# Revit family: RN 81046 Optipress-Aquaplus-Vis de rappel
name_source: partatom
category: Rohrformteile
units: mm (PartAtom-declared; Revit-internal decimal feet)

## family parameters
Arbeitsebenenbasiert = Nein
Beim Laden mit Abzugskörper schneiden = Nein
Bemaßung runder Anschluss = Durchmesser verwenden
Gemeinsam genutzt = Nein
Immer vertikal = Ja
Teiletyp = Verbindung

## types (12) — shared parameters
1.010.00.2 Numéro de feuille de la directive = 29
1.010.00.3 Date de publication (mois) de la ligne directrice = 201308
1.010.00.4 Nom du Fabricant = R. Nussbaum AG
1.010.00.5 Date de révision du fichier = 20190521
1.010.00.6 Adresse Web du fabricant = http://www.nussbaum.ch
1.100.00.4 Désignation du produit = Alimentation
1.110.00.2 Indice = 4
1.110.00.4 Désignation du produit = Optipress
1.960/3L.00.8 Lien (URL) = https://www.nussbaum.ch
29.700.00.4 Nom du produit = Optipress-Aquaplus-Vis de rappel, avec filetage mâle
29.700.00.5 Identification du produit = 2
29.700.00.6 Forme transversale = 1
29.700.00.7 Système de taille nominale = DN
29.700.00.8 Système de pression nominale = PN
29.710.02.4 Pression nominale = 16
29.710.02.5 Max. [hPa] = 1600
29.710.02.7 Max. [hPa] = 1600
29.710.02.9 Max. [°C] = 95
Connector Visibility = Nein
EnclosingSpace Visibility = Nein

## per-type parameters (varying)
- 81046.21, Optipress-Aquaplus-Vis de rappel, avec filetage mâle, DN=15x20, L=67, R=¾: 1.800.00.3 Numéro BS=01900400000000000000000000000000000000000000000028000000000000000012; 1.810.00.3 Numéro de commande fabricant=81046.21; 1.810.00.4 Numéro DATANORM=81046.21; 1.810.00.6 Numéro GTIN=7612945022196; 29.710.02.10 Poids d'ajustement [kg]=0.139; 29.710.02.3 La désignation=Optipress-Aquaplus-Vis de rappel, avec filetage mâle, DN=15x20, L=67, R=¾; CONNECTOR0_DIAMETER_dX_0r=15 mm  [stored 0.0492126 ft]; CONNECTOR0_dX_01=22 mm; CONNECTOR0_ref_dX=22 mm; CONNECTOR1_DIAMETER_dX_0r=20 mm; CONNECTOR1_dX_00=48 mm; CONNECTOR1_dX_01=63 mm; CONNECTOR1_ref_dX=48 mm; R. Nussbaum AG 81046.20 fr Visibility=Nein; R. Nussbaum AG 81046.21 fr Visibility=Ja; R. Nussbaum AG 81046.22 fr Visibility=Nein; R. Nussbaum AG 81046.23 fr Visibility=Nein; R. Nussbaum AG 81046.24 fr Visibility=Nein; R. Nussbaum AG 81046.25 fr Visibility=Nein; R. Nussbaum AG 81046.27 fr Visibility=Nein; R. Nussbaum AG 81046.28 fr Visibility=Nein; R. Nussbaum AG 81046.29 fr Visibility=Nein; R. Nussbaum AG 81046.31 fr Visibility=Nein; R. Nussbaum AG 81046.33 fr Visibility=Nein; R. Nussbaum AG 81046.34 fr Visibility=Nein
- 81046.22, Optipress-Aquaplus-Vis de rappel, avec filetage mâle, DN=15, L=67, R=½: 1.800.00.3 Numéro BS=01900400000000000000000000000000000000000000000028000000000000000013; 1.810.00.3 Numéro de commande fabricant=81046.22; 1.810.00.4 Numéro DATANORM=81046.22; 1.810.00.5 Numéro StLB=266.333; 1.810.00.6 Numéro GTIN=7612945022202; 29.710.02.10 Poids d'ajustement [kg]=0.129; 29.710.02.3 La désignation=Optipress-Aquaplus-Vis de rappel, avec filetage mâle, DN=15, L=67, R=½; CONNECTOR0_DIAMETER_dX_0r=15 mm  [stored 0.0492126 ft]; CONNECTOR0_dX_01=22 mm; CONNECTOR0_ref_dX=22 mm; CONNECTOR1_DIAMETER_dX_0r=15 mm  [stored 0.0492126 ft]; CONNECTOR1_dX_00=50 mm; CONNECTOR1_dX_01=63 mm; CONNECTOR1_ref_dX=50 mm; R. Nussbaum AG 81046.20 fr Visibility=Nein; R. Nussbaum AG 81046.21 fr Visibility=Nein; R. Nussbaum AG 81046.22 fr Visibility=Ja; R. Nussbaum AG 81046.23 fr Visibility=Nein; R. Nussbaum AG 81046.24 fr Visibility=Nein; R. Nussbaum AG 81046.25 fr Visibility=Nein; R. Nussbaum AG 81046.27 fr Visibility=Nein; R. Nussbaum AG 81046.28 fr Visibility=Nein; R. Nussbaum AG 81046.29 fr Visibility=Nein; R. Nussbaum AG 81046.31 fr Visibility=Nein; R. Nussbaum AG 81046.33 fr Visibility=Nein; R. Nussbaum AG 81046.34 fr Visibility=Nein
- 81046.23, Optipress-Aquaplus-Vis de rappel, avec filetage mâle, DN=15x20, L=69, R=¾: 1.800.00.3 Numéro BS=01900400000000000000000000000000000000000000000028000000000000000014; 1.810.00.3 Numéro de commande fabricant=81046.23; 1.810.00.4 Numéro DATANORM=81046.23; 1.810.00.6 Numéro GTIN=7612945022219; 29.710.02.10 Poids d'ajustement [kg]=0.139; 29.710.02.3 La désignation=Optipress-Aquaplus-Vis de rappel, avec filetage mâle, DN=15x20, L=69, R=¾; CONNECTOR0_DIAMETER_dX_0r=15 mm  [stored 0.0492126 ft]; CONNECTOR0_dX_01=22 mm; CONNECTOR0_ref_dX=22 mm; CONNECTOR1_DIAMETER_dX_0r=20 mm; CONNECTOR1_dX_00=50 mm; CONNECTOR1_dX_01=65 mm; CONNECTOR1_ref_dX=50 mm; R. Nussbaum AG 81046.20 fr Visibility=Nein; R. Nussbaum AG 81046.21 fr Visibility=Nein; R. Nussbaum AG 81046.22 fr Visibility=Nein; R. Nussbaum AG 81046.23 fr Visibility=Ja; R. Nussbaum AG 81046.24 fr Visibility=Nein; R. Nussbaum AG 81046.25 fr Visibility=Nein; R. Nussbaum AG 81046.27 fr Visibility=Nein; R. Nussbaum AG 81046.28 fr Visibility=Nein; R. Nussbaum AG 81046.29 fr Visibility=Nein; R. Nussbaum AG 81046.31 fr Visibility=Nein; R. Nussbaum AG 81046.33 fr Visibility=Nein; R. Nussbaum AG 81046.34 fr Visibility=Nein
- 81046.24, Optipress-Aquaplus-Vis de rappel, avec filetage mâle, DN=20x15, L=80, R=½: 1.800.00.3 Numéro BS=01900400000000000000000000000000000000000000000028000000000000000015; 1.810.00.3 Numéro de commande fabricant=81046.24; 1.810.00.4 Numéro DATANORM=81046.24; 1.810.00.6 Numéro GTIN=7612945022226; 29.710.02.10 Poids d'ajustement [kg]=0.149; 29.710.02.3 La désignation=Optipress-Aquaplus-Vis de rappel, avec filetage mâle, DN=20x15, L=80, R=½; CONNECTOR0_DIAMETER_dX_0r=20 mm; CONNECTOR0_dX_01=24 mm; CONNECTOR0_ref_dX=24 mm; CONNECTOR1_DIAMETER_dX_0r=15 mm  [stored 0.0492126 ft]; CONNECTOR1_dX_00=58 mm; CONNECTOR1_dX_01=71 mm; CONNECTOR1_ref_dX=58 mm; R. Nussbaum AG 81046.20 fr Visibility=Nein; R. Nussbaum AG 81046.21 fr Visibility=Nein; R. Nussbaum AG 81046.22 fr Visibility=Nein; R. Nussbaum AG 81046.23 fr Visibility=Nein; R. Nussbaum AG 81046.24 fr Visibility=Ja; R. Nussbaum AG 81046.25 fr Visibility=Nein; R. Nussbaum AG 81046.27 fr Visibility=Nein; R. Nussbaum AG 81046.28 fr Visibility=Nein; R. Nussbaum AG 81046.29 fr Visibility=Nein; R. Nussbaum AG 81046.31 fr Visibility=Nein; R. Nussbaum AG 81046.33 fr Visibility=Nein; R. Nussbaum AG 81046.34 fr Visibility=Nein
- 81046.25, Optipress-Aquaplus-Vis de rappel, avec filetage mâle, DN=20, L=81, R=¾: 1.800.00.3 Numéro BS=01900400000000000000000000000000000000000000000028000000000000000016; 1.810.00.3 Numéro de commande fabricant=81046.25; 1.810.00.4 Numéro DATANORM=81046.25; 1.810.00.5 Numéro StLB=266.334; 1.810.00.6 Numéro GTIN=7612945022233; 29.710.02.10 Poids d'ajustement [kg]=0.209; 29.710.02.3 La désignation=Optipress-Aquaplus-Vis de rappel, avec filetage mâle, DN=20, L=81, R=¾; CONNECTOR0_DIAMETER_dX_0r=20 mm; CONNECTOR0_dX_01=24 mm; CONNECTOR0_ref_dX=24 mm; CONNECTOR1_DIAMETER_dX_0r=20 mm; CONNECTOR1_dX_00=53 mm; CONNECTOR1_dX_01=68 mm; CONNECTOR1_ref_dX=53 mm; R. Nussbaum AG 81046.20 fr Visibility=Nein; R. Nussbaum AG 81046.21 fr Visibility=Nein; R. Nussbaum AG 81046.22 fr Visibility=Nein; R. Nussbaum AG 81046.23 fr Visibility=Nein; R. Nussbaum AG 81046.24 fr Visibility=Nein; R. Nussbaum AG 81046.25 fr Visibility=Ja; R. Nussbaum AG 81046.27 fr Visibility=Nein; R. Nussbaum AG 81046.28 fr Visibility=Nein; R. Nussbaum AG 81046.29 fr Visibility=Nein; R. Nussbaum AG 81046.31 fr Visibility=Nein; R. Nussbaum AG 81046.33 fr Visibility=Nein; R. Nussbaum AG 81046.34 fr Visibility=Nein
- 81046.27, Optipress-Aquaplus-Vis de rappel, avec filetage mâle, DN=20x25, L=84, R=1: 1.800.00.3 Numéro BS=01900400000000000000000000000000000000000000000028000000000000000017; 1.810.00.3 Numéro de commande fabricant=81046.27; 1.810.00.4 Numéro DATANORM=81046.27; 1.810.00.6 Numéro GTIN=7612945022240; 29.710.02.10 Poids d'ajustement [kg]=0.212; 29.710.02.3 La désignation=Optipress-Aquaplus-Vis de rappel, avec filetage mâle, DN=20x25, L=84, R=1; CONNECTOR0_DIAMETER_dX_0r=20 mm; CONNECTOR0_dX_01=24 mm; CONNECTOR0_ref_dX=24 mm; CONNECTOR1_DIAMETER_dX_0r=25 mm  [stored 0.082021 ft]; CONNECTOR1_dX_00=54 mm; CONNECTOR1_dX_01=71 mm; CONNECTOR1_ref_dX=54 mm; R. Nussbaum AG 81046.20 fr Visibility=Nein; R. Nussbaum AG 81046.21 fr Visibility=Nein; R. Nussbaum AG 81046.22 fr Visibility=Nein; R. Nussbaum AG 81046.23 fr Visibility=Nein; R. Nussbaum AG 81046.24 fr Visibility=Nein; R. Nussbaum AG 81046.25 fr Visibility=Nein; R. Nussbaum AG 81046.27 fr Visibility=Ja; R. Nussbaum AG 81046.28 fr Visibility=Nein; R. Nussbaum AG 81046.29 fr Visibility=Nein; R. Nussbaum AG 81046.31 fr Visibility=Nein; R. Nussbaum AG 81046.33 fr Visibility=Nein; R. Nussbaum AG 81046.34 fr Visibility=Nein
- 81046.28, Optipress-Aquaplus-Vis de rappel, avec filetage mâle, DN=25x20, L=82, R=¾: 1.800.00.3 Numéro BS=01900400000000000000000000000000000000000000000028000000000000000018; 1.810.00.3 Numéro de commande fabricant=81046.28; 1.810.00.4 Numéro DATANORM=81046.28; 1.810.00.6 Numéro GTIN=7612945682802; 29.710.02.10 Poids d'ajustement [kg]=0.319; 29.710.02.3 La désignation=Optipress-Aquaplus-Vis de rappel, avec filetage mâle, DN=25x20, L=82, R=¾; CONNECTOR0_DIAMETER_dX_0r=25 mm  [stored 0.082021 ft]; CONNECTOR0_dX_01=24 mm; CONNECTOR0_ref_dX=24 mm; CONNECTOR1_DIAMETER_dX_0r=20 mm; CONNECTOR1_dX_00=64 mm; CONNECTOR1_dX_01=79 mm; CONNECTOR1_ref_dX=64 mm; R. Nussbaum AG 81046.20 fr Visibility=Nein; R. Nussbaum AG 81046.21 fr Visibility=Nein; R. Nussbaum AG 81046.22 fr Visibility=Nein; R. Nussbaum AG 81046.23 fr Visibility=Nein; R. Nussbaum AG 81046.24 fr Visibility=Nein; R. Nussbaum AG 81046.25 fr Visibility=Nein; R. Nussbaum AG 81046.27 fr Visibility=Nein; R. Nussbaum AG 81046.28 fr Visibility=Ja; R. Nussbaum AG 81046.29 fr Visibility=Nein; R. Nussbaum AG 81046.31 fr Visibility=Nein; R. Nussbaum AG 81046.33 fr Visibility=Nein; R. Nussbaum AG 81046.34 fr Visibility=Nein
- 81046.29, Optipress-Aquaplus-Vis de rappel, avec filetage mâle, DN=25, L=78, R=1: 1.800.00.3 Numéro BS=01900400000000000000000000000000000000000000000028000000000000000019; 1.810.00.3 Numéro de commande fabricant=81046.29; 1.810.00.4 Numéro DATANORM=81046.29; 1.810.00.5 Numéro StLB=266.335; 1.810.00.6 Numéro GTIN=7612945022257; 29.710.02.10 Poids d'ajustement [kg]=0.311; 29.710.02.3 La désignation=Optipress-Aquaplus-Vis de rappel, avec filetage mâle, DN=25, L=78, R=1; CONNECTOR0_DIAMETER_dX_0r=25 mm  [stored 0.082021 ft]; CONNECTOR0_dX_01=24 mm; CONNECTOR0_ref_dX=24 mm; CONNECTOR1_DIAMETER_dX_0r=25 mm  [stored 0.082021 ft]; CONNECTOR1_dX_00=58 mm; CONNECTOR1_dX_01=75 mm; CONNECTOR1_ref_dX=58 mm; R. Nussbaum AG 81046.20 fr Visibility=Nein; R. Nussbaum AG 81046.21 fr Visibility=Nein; R. Nussbaum AG 81046.22 fr Visibility=Nein; R. Nussbaum AG 81046.23 fr Visibility=Nein; R. Nussbaum AG 81046.24 fr Visibility=Nein; R. Nussbaum AG 81046.25 fr Visibility=Nein; R. Nussbaum AG 81046.27 fr Visibility=Nein; R. Nussbaum AG 81046.28 fr Visibility=Nein; R. Nussbaum AG 81046.29 fr Visibility=Ja; R. Nussbaum AG 81046.31 fr Visibility=Nein; R. Nussbaum AG 81046.33 fr Visibility=Nein; R. Nussbaum AG 81046.34 fr Visibility=Nein
- 81046.31, Optipress-Aquaplus-Vis de rappel, avec filetage mâle, DN=32, L=101, R=1¼: 1.800.00.3 Numéro BS=01900400000000000000000000000000000000000000000028000000000000000020; 1.810.00.3 Numéro de commande fabricant=81046.31; 1.810.00.4 Numéro DATANORM=81046.31; 1.810.00.5 Numéro StLB=266.336; 1.810.00.6 Numéro GTIN=7612945022264; 29.710.02.10 Poids d'ajustement [kg]=0.439; 29.710.02.3 La désignation=Optipress-Aquaplus-Vis de rappel, avec filetage mâle, DN=32, L=101, R=1¼; CONNECTOR0_DIAMETER_dX_0r=32 mm  [stored 0.104987 ft]; CONNECTOR0_dX_01=26 mm; CONNECTOR0_ref_dX=26 mm; CONNECTOR1_DIAMETER_dX_0r=32 mm  [stored 0.104987 ft]; CONNECTOR1_dX_00=66 mm; CONNECTOR1_dX_01=85 mm; CONNECTOR1_ref_dX=66 mm; R. Nussbaum AG 81046.20 fr Visibility=Nein; R. Nussbaum AG 81046.21 fr Visibility=Nein; R. Nussbaum AG 81046.22 fr Visibility=Nein; R. Nussbaum AG 81046.23 fr Visibility=Nein; R. Nussbaum AG 81046.24 fr Visibility=Nein; R. Nussbaum AG 81046.25 fr Visibility=Nein; R. Nussbaum AG 81046.27 fr Visibility=Nein; R. Nussbaum AG 81046.28 fr Visibility=Nein; R. Nussbaum AG 81046.29 fr Visibility=Nein; R. Nussbaum AG 81046.31 fr Visibility=Ja; R. Nussbaum AG 81046.33 fr Visibility=Nein; R. Nussbaum AG 81046.34 fr Visibility=Nein
- 81046.33, Optipress-Aquaplus-Vis de rappel, avec filetage mâle, DN=40, L=101, R=1½: 1.800.00.3 Numéro BS=01900400000000000000000000000000000000000000000028000000000000000021; 1.810.00.3 Numéro de commande fabricant=81046.33; 1.810.00.4 Numéro DATANORM=81046.33; 1.810.00.5 Numéro StLB=266.337; 1.810.00.6 Numéro GTIN=7612945022271; 29.710.02.10 Poids d'ajustement [kg]=0.591; 29.710.02.3 La désignation=Optipress-Aquaplus-Vis de rappel, avec filetage mâle, DN=40, L=101, R=1½; CONNECTOR0_DIAMETER_dX_0r=40 mm; CONNECTOR0_dX_01=36 mm; CONNECTOR0_ref_dX=36 mm; CONNECTOR1_DIAMETER_dX_0r=40 mm; CONNECTOR1_dX_00=83 mm; CONNECTOR1_dX_01=102 mm; CONNECTOR1_ref_dX=83 mm; R. Nussbaum AG 81046.20 fr Visibility=Nein; R. Nussbaum AG 81046.21 fr Visibility=Nein; R. Nussbaum AG 81046.22 fr Visibility=Nein; R. Nussbaum AG 81046.23 fr Visibility=Nein; R. Nussbaum AG 81046.24 fr Visibility=Nein; R. Nussbaum AG 81046.25 fr Visibility=Nein; R. Nussbaum AG 81046.27 fr Visibility=Nein; R. Nussbaum AG 81046.28 fr Visibility=Nein; R. Nussbaum AG 81046.29 fr Visibility=Nein; R. Nussbaum AG 81046.31 fr Visibility=Nein; R. Nussbaum AG 81046.33 fr Visibility=Ja; R. Nussbaum AG 81046.34 fr Visibility=Nein
- 81046.34, Optipress-Aquaplus-Vis de rappel, avec filetage mâle, DN=50, L=107, R=2: 1.800.00.3 Numéro BS=01900400000000000000000000000000000000000000000028000000000000000022; 1.810.00.3 Numéro de commande fabricant=81046.34; 1.810.00.4 Numéro DATANORM=81046.34; 1.810.00.5 Numéro StLB=266.338; 1.810.00.6 Numéro GTIN=7612945022288; 29.710.02.10 Poids d'ajustement [kg]=0.981; 29.710.02.3 La désignation=Optipress-Aquaplus-Vis de rappel, avec filetage mâle, DN=50, L=107, R=2; CONNECTOR0_DIAMETER_dX_0r=50 mm; CONNECTOR0_dX_01=40 mm; CONNECTOR0_ref_dX=40 mm; CONNECTOR1_DIAMETER_dX_0r=50 mm; CONNECTOR1_dX_00=84 mm; CONNECTOR1_dX_01=108 mm; CONNECTOR1_ref_dX=84 mm; R. Nussbaum AG 81046.20 fr Visibility=Nein; R. Nussbaum AG 81046.21 fr Visibility=Nein; R. Nussbaum AG 81046.22 fr Visibility=Nein; R. Nussbaum AG 81046.23 fr Visibility=Nein; R. Nussbaum AG 81046.24 fr Visibility=Nein; R. Nussbaum AG 81046.25 fr Visibility=Nein; R. Nussbaum AG 81046.27 fr Visibility=Nein; R. Nussbaum AG 81046.28 fr Visibility=Nein; R. Nussbaum AG 81046.29 fr Visibility=Nein; R. Nussbaum AG 81046.31 fr Visibility=Nein; R. Nussbaum AG 81046.33 fr Visibility=Nein; R. Nussbaum AG 81046.34 fr Visibility=Ja
- 81046.20, Optipress-Aquaplus-Vis de rappel, avec filetage mâle, DN=12x15, L=65, R=½: 1.800.00.3 Numéro BS=01900400000000000000000000000000000000000000000028000000000000000024; 1.810.00.3 Numéro de commande fabricant=81046.20; 1.810.00.4 Numéro DATANORM=81046.20; 1.810.00.5 Numéro StLB=266.332; 1.810.00.6 Numéro GTIN=7612945022189; 29.710.02.10 Poids d'ajustement [kg]=0.129; 29.710.02.3 La désignation=Optipress-Aquaplus-Vis de rappel, avec filetage mâle, DN=12x15, L=65, R=½; CONNECTOR0_DIAMETER_dX_0r=12 mm  [stored 0.0393701 ft]; CONNECTOR0_dX_01=22 mm; CONNECTOR0_ref_dX=22 mm; CONNECTOR1_DIAMETER_dX_0r=15 mm  [stored 0.0492126 ft]; CONNECTOR1_dX_00=48 mm; CONNECTOR1_dX_01=61 mm; CONNECTOR1_ref_dX=48 mm; R. Nussbaum AG 81046.20 fr Visibility=Ja; R. Nussbaum AG 81046.21 fr Visibility=Nein; R. Nussbaum AG 81046.22 fr Visibility=Nein; R. Nussbaum AG 81046.23 fr Visibility=Nein; R. Nussbaum AG 81046.24 fr Visibility=Nein; R. Nussbaum AG 81046.25 fr Visibility=Nein; R. Nussbaum AG 81046.27 fr Visibility=Nein; R. Nussbaum AG 81046.28 fr Visibility=Nein; R. Nussbaum AG 81046.29 fr Visibility=Nein; R. Nussbaum AG 81046.31 fr Visibility=Nein; R. Nussbaum AG 81046.33 fr Visibility=Nein; R. Nussbaum AG 81046.34 fr Visibility=Nein

note: column(s) folded — value = type name in every type: 1.800.00.4 Champ de commentaires

note: [stored X ft] marks values corroborated as IEEE doubles in the binary element streams (Revit-internal decimal feet)

## geometry (parser evidence)
native form markers: Sweep x2
no freeform markers — native parametric forms only
